# Revit family: DW24UT2I3 DRAFT
name_source: partatom
category: Specialty Equipment
units: mm (PartAtom-declared; Revit-internal decimal feet)

## family parameters
Always vertical = No
Cut with Voids When Loaded = Yes
Part Type = Normal
Room Calculation Point = No
Round Connector Dimension = Use Diameter
Shared = No
Work Plane-Based = Yes

## types (1)
- DW24UT2I3
    Cavity - Depth = 560 mm  [stored 1.83727 ft]
    Cavity - Height = 860 mm
    Cavity - Width = 600 mm
    Default Elevation = 0 mm  [stored 0 ft]
    Description = Series 7, Integrated Tall Dishwasher
    Manufacturer = Fisher & Paykel Appliances
    Model = DW24UT2I3
    Product - Depth = 560 mm  [stored 1.83727 ft]
    Product - Minimum Height (857mm - 917mm) = 857 mm  [stored 2.81168 ft]
    Product - Width = 598 mm
    URL = www.fisherpaykel.com

note: [stored X ft] marks values corroborated as IEEE doubles in the binary element streams (Revit-internal decimal feet)

## geometry (parser evidence)
native form markers: Sweep x103
no freeform markers — native parametric forms only
